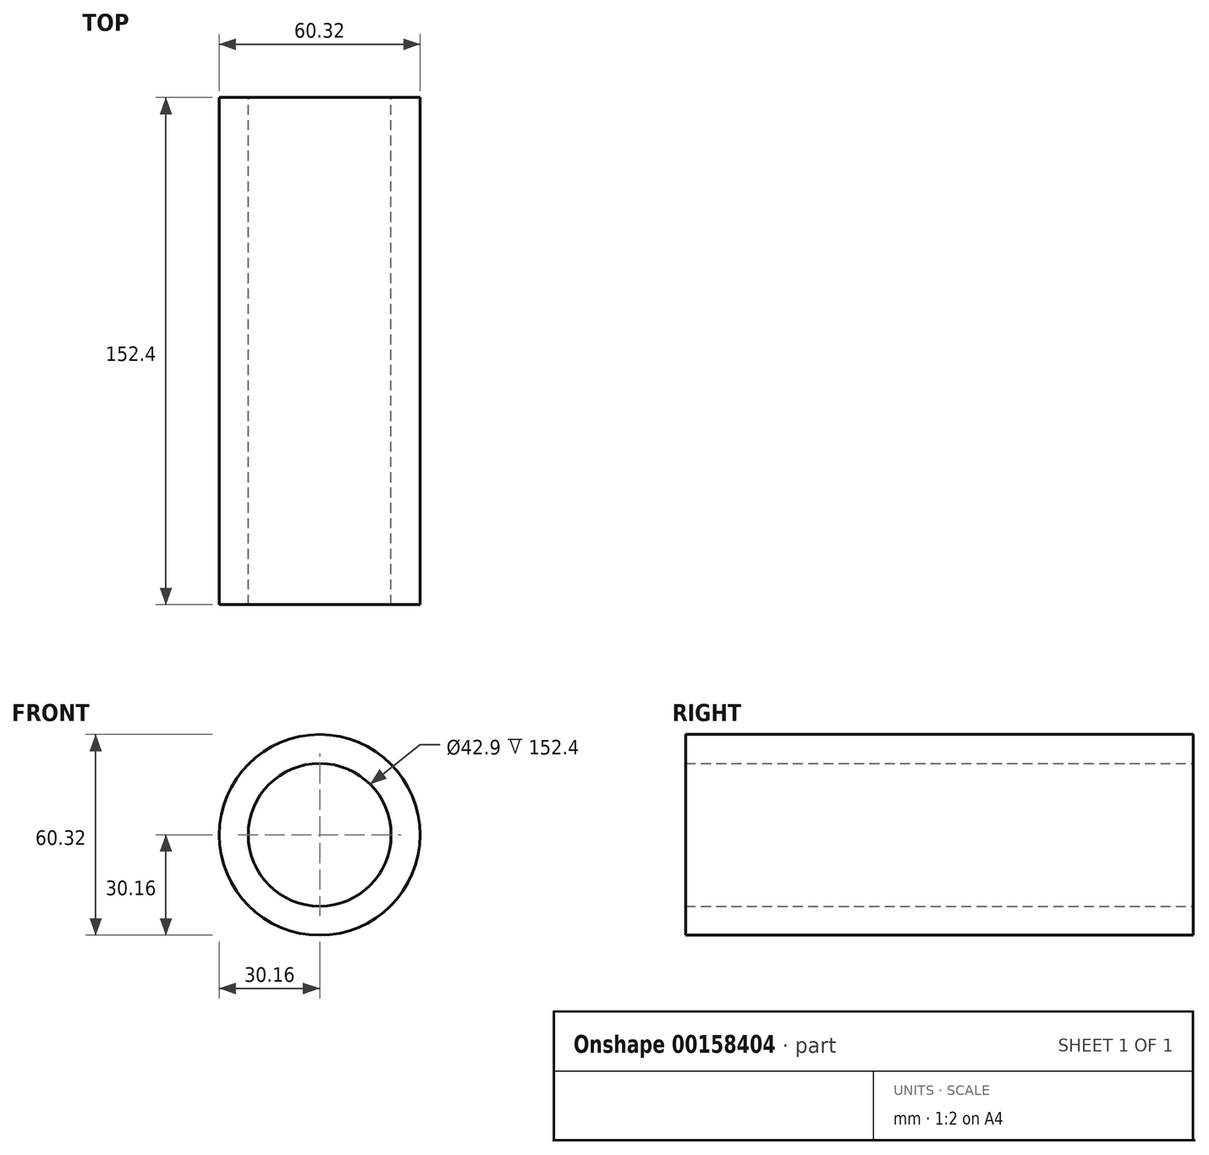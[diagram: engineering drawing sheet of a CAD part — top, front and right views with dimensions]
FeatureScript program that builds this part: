
annotation { "Feature Type Name" : "Feature", "Feature Type Description" : "" }
export const myFeature = defineFeature(function(context is Context, id is Id, definition is map)
    precondition{}
    {
        {
            var Q0;
            Q0=qCreatedBy(makeId("Front.planeOp"),FACE);
            var sketch = newSketch(context, id + "F0", { "sketchPlane" : qUnion([Q0])});
            skCircle(sketch, "E0", {"center": v(0, 0) * mm, "radius": 30.16 * mm});
            skCircle(sketch, "E1.0", {"center": v(0, 0) * mm, "radius": 21.45 * mm});
            skSolve(sketch);
        }
        {
            var Q0;
            Q0=makeQuery(id+"F0.imprint","IMPRINT",FACE,{"disambiguationData":[TD([[makeQuery(id+"F0.imprint","IMPRINT",EDGE,{"derivedFrom":sQuery(id+"F0.wireOp",EDGE,"E0")}),1.0]])]});
            extrude(context, id + "F1", {"entities" : qUnion([Q0]), "depth" : 152.4 * mm});
        }
    });
